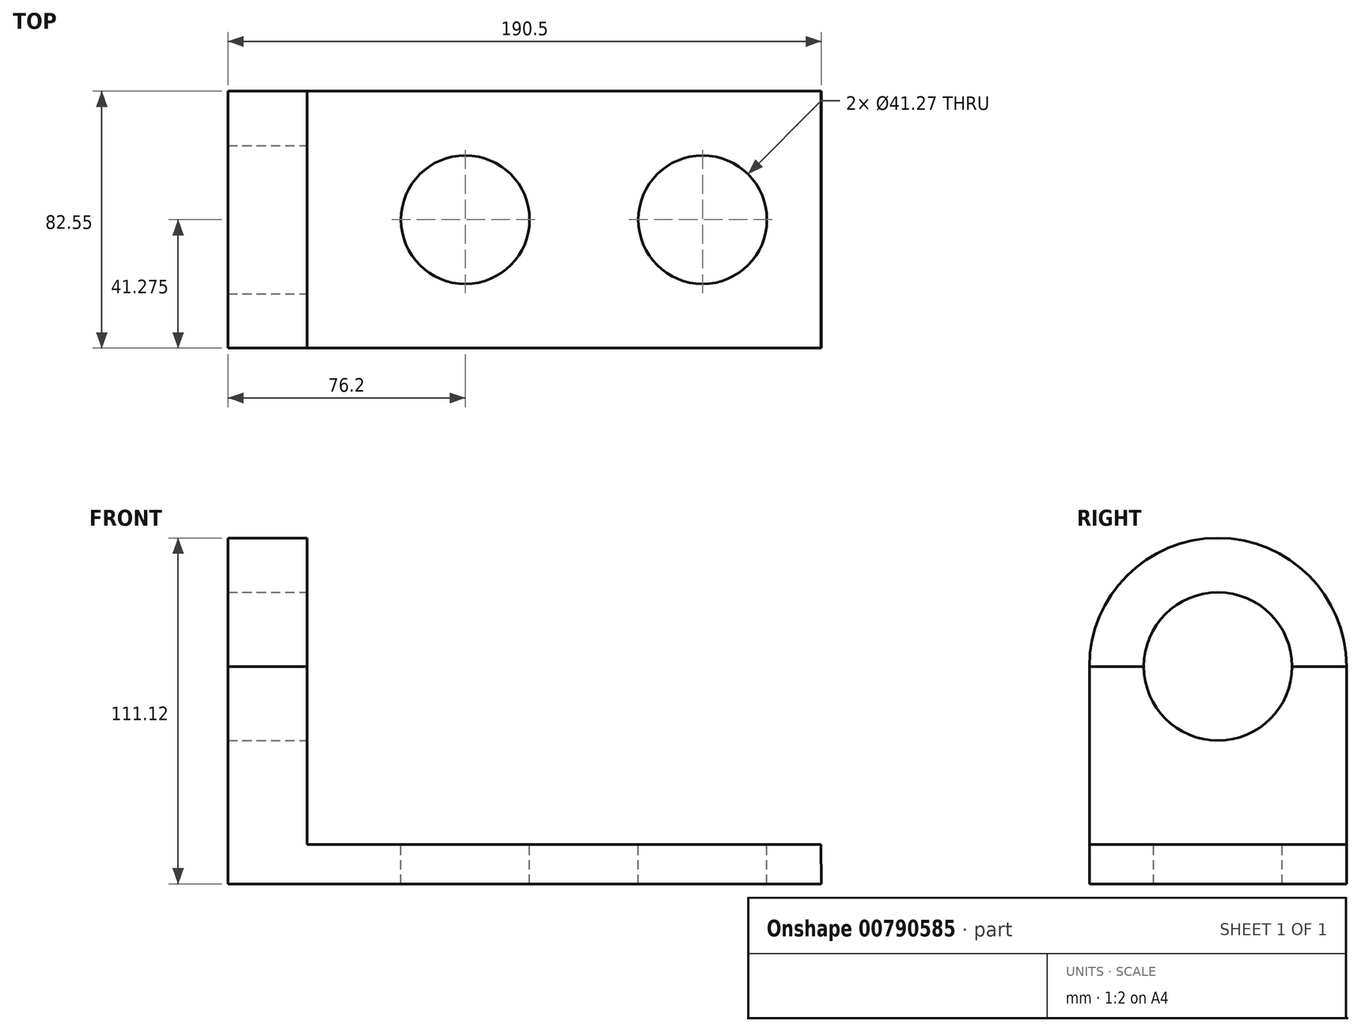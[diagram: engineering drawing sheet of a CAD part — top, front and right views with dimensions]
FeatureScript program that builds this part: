
annotation { "Feature Type Name" : "Feature", "Feature Type Description" : "" }
export const myFeature = defineFeature(function(context is Context, id is Id, definition is map)
    precondition{}
    {
        {
            var Q0;
            Q0=qCreatedBy(makeId("Front.planeOp"),FACE);
            var sketch = newSketch(context, id + "F0", { "sketchPlane" : qUnion([Q0])});
            skLineSegment(sketch, "E0", {"start": v(0, 0) * mm, "end": v(190.5, 0) * mm});
            skLineSegment(sketch, "E1", {"start": v(0, 0) * mm, "end": v(0, 12.7) * mm});
            skLineSegment(sketch, "E2", {"start": v(0, 12.7) * mm, "end": v(190.32, 12.7) * mm});
            skLineSegment(sketch, "E3", {"start": v(190.32, 12.7) * mm, "end": v(190.5, 0) * mm});
            skSolve(sketch);
        }
        {
            var Q0;
            Q0 = qSketchRegion(id + "F0", true);
            extrude(context, id + "F1", {"entities" : qUnion([Q0]), "depth" : 82.55 * mm, "offsetDistance" : 25.4 * mm});
        }
        {
            var Q0;
            Q0=makeQuery(id+"F1.opExtrude","SWEPT_FACE",FACE,{"disambiguationData":[OSD([sQuery(id+"F0.wireOp",EDGE,"E2")])]});
            var sketch = newSketch(context, id + "F2", { "sketchPlane" : qUnion([Q0])});
            skLineSegment(sketch, "E4", {"start": v(0, -82.55) * mm, "end": v(25.4, -82.55) * mm});
            skLineSegment(sketch, "E5", {"start": v(25.4, -82.55) * mm, "end": v(25.4, 0) * mm});
            skSolve(sketch);
        }
        {
            var Q0;
            Q0 = qSketchRegion(id + "F2", true);
            var Q1;
            Q1=makeQuery(id+"F2.imprint","IMPRINT",FACE,{"disambiguationData":[TD([[makeQuery(id+"F2.imprint","IMPRINT",EDGE,{"derivedFrom":sQuery(id+"F2.wireOp",EDGE,"E4")}),1.0]])]});
            extrude(context, id + "F3", {"entities" : qUnion([Q0, Q1]), "operationType" : NewBodyOperationType.ADD, "depth" : 57.15 * mm, "offsetDistance" : 25.4 * mm});
        }
        {
            var Q0;
            Q0=makeQuery(id+"F3.opExtrude","SWEPT_FACE",FACE,{"disambiguationData":[OSD([sQuery(id+"F2.wireOp",EDGE,"E5")])]});
            var sketch = newSketch(context, id + "F4", { "sketchPlane" : qUnion([Q0])});
            skLineSegment(sketch, "E6", {"start": v(-41.28, 69.85) * mm, "end": v(0, 69.85) * mm, "construction": true});
            skLineSegment(sketch, "E7", {"start": v(-43.98, 69.85) * mm, "end": v(-82.55, 69.85) * mm, "construction": true});
            skArc(sketch, "E8", {"start": v(0, 69.85) * mm, "mid": v(-41.28, 111.13) * mm, "end": v(-82.55, 69.85) * mm});
            skSolve(sketch);
        }
        {
            var Q0;
            Q0 = qSketchRegion(id + "F4", true);
            var Q1;
            Q1=makeQuery(id+"F4.imprint","IMPRINT",FACE,{"disambiguationData":[TD([[makeQuery(id+"F4.imprint","IMPRINT",EDGE,{"derivedFrom":sQuery(id+"F4.wireOp",EDGE,"E8")}),1.0]])]});
            extrude(context, id + "F5", {"entities" : qUnion([Q0, Q1]), "oppositeDirection" : true, "depth" : 25.4 * mm, "offsetDistance" : 25.4 * mm});
        }
        {
            var Q0;
            Q0=makeQuery(id+"F3.opExtrude","SWEPT_FACE",FACE,{"disambiguationData":[OSD([sQuery(id+"F2.wireOp",EDGE,"E5")])]});
            var sketch = newSketch(context, id + "F6", { "sketchPlane" : qUnion([Q0])});
            skCircle(sketch, "E9", {"center": v(-41.28, 69.85) * mm, "radius": 23.81 * mm});
            skSolve(sketch);
        }
        {
            var Q0;
            Q0=makeQuery(id+"F5.opExtrude","CAP_FACE",FACE,{"disambiguationData":[OSD([sQuery(id+"F2.wireOp",EDGE,"E5"),sQuery(id+"F4.wireOp",EDGE,"E8")])],"isStart":true});
            var sketch = newSketch(context, id + "F7", { "sketchPlane" : qUnion([Q0])});
            skCircle(sketch, "E10", {"center": v(-41.28, 69.85) * mm, "radius": 23.81 * mm});
            skSolve(sketch);
        }
        {
            var Q0;
            Q0 = qSketchRegion(id + "F7", true);
            var Q1;
            Q1 = qSketchRegion(id + "F6", true);
            var Q2;
            {var subQ0=sQuery(id+"F6.wireOp",EDGE,"E9");var subQ1=makeQuery(id+"F3.opExtrude","CAP_EDGE",EDGE,{"disambiguationData":[OSD([sQuery(id+"F2.wireOp",EDGE,"E5")])],"isStart":false});var subQ2=makeQuery(id+"F6.imprint","INTERSECT",VERTEX,{"disambiguationData":[OD(0.0)],"derivedFrom":[subQ1,subQ0]});Q2=makeQuery(id+"F6.imprint","IMPRINT",FACE,{"disambiguationData":[TD([[makeQuery(id+"F6.imprint","IMPRINT",EDGE,{"disambiguationData":[TD([[subQ2,1.0]])],"derivedFrom":subQ0}),1.0]])]});}
            var Q3;
            {var subQ0=sQuery(id+"F6.wireOp",EDGE,"E9");var subQ1=makeQuery(id+"F3.opExtrude","CAP_EDGE",EDGE,{"disambiguationData":[OSD([sQuery(id+"F2.wireOp",EDGE,"E5")])],"isStart":false});var subQ2=makeQuery(id+"F6.imprint","INTERSECT",VERTEX,{"disambiguationData":[OD(0.0)],"derivedFrom":[subQ1,subQ0]});Q3=makeQuery(id+"F6.imprint","IMPRINT",FACE,{"disambiguationData":[TD([[makeQuery(id+"F6.imprint","IMPRINT",EDGE,{"disambiguationData":[TD([[subQ2,-1.0]])],"derivedFrom":subQ0}),1.0]])]});}
            extrude(context, id + "F8", {"entities" : qUnion([Q0, Q1, Q2, Q3]), "operationType" : NewBodyOperationType.REMOVE, "endBound" : BoundingType.THROUGH_ALL, "oppositeDirection" : true, "depth" : 50.8 * mm, "offsetDistance" : 25.4 * mm});
        }
        {
            var Q0;
            Q0 = qSketchRegion(id + "F6", true);
            extrude(context, id + "F9", {"entities" : qUnion([Q0]), "operationType" : NewBodyOperationType.REMOVE, "endBound" : BoundingType.THROUGH_ALL, "oppositeDirection" : true, "depth" : 25.4 * mm, "offsetDistance" : 25.4 * mm});
        }
        {
            var Q0;
            Q0=makeQuery(id+"F1.opExtrude","SWEPT_FACE",FACE,{"disambiguationData":[OSD([sQuery(id+"F0.wireOp",EDGE,"E2")])]});
            var sketch = newSketch(context, id + "F10", { "sketchPlane" : qUnion([Q0])});
            skLineSegment(sketch, "E11", {"start": v(25.4, -41.28) * mm, "end": v(76.2, -41.28) * mm, "construction": true});
            skLineSegment(sketch, "E12", {"start": v(76.2, -41.28) * mm, "end": v(152.4, -41.28) * mm, "construction": true});
            skCircle(sketch, "E13", {"center": v(76.2, -41.28) * mm, "radius": 20.64 * mm});
            skCircle(sketch, "E14", {"center": v(152.4, -41.28) * mm, "radius": 20.64 * mm});
            skSolve(sketch);
        }
        {
            var Q0;
            Q0=makeQuery(id+"F10.imprint","IMPRINT",FACE,{"disambiguationData":[TD([[makeQuery(id+"F10.imprint","IMPRINT",EDGE,{"derivedFrom":sQuery(id+"F10.wireOp",EDGE,"E13")}),1.0]])]});
            var Q1;
            Q1=makeQuery(id+"F10.imprint","IMPRINT",FACE,{"disambiguationData":[TD([[makeQuery(id+"F10.imprint","IMPRINT",EDGE,{"derivedFrom":sQuery(id+"F10.wireOp",EDGE,"E14")}),1.0]])]});
            extrude(context, id + "F11", {"entities" : qUnion([Q0, Q1]), "operationType" : NewBodyOperationType.REMOVE, "oppositeDirection" : true, "depth" : 25.4 * mm, "offsetDistance" : 25.4 * mm});
        }
    });
